# Revit family: Electronics_Community-Point-Source_Biamp_Loudspeaker_IC6_1062
name_source: partatom
category: Communication Devices
units: mm (PartAtom-declared; Revit-internal decimal feet)

## family parameters
Cut with Voids When Loaded = No
Host = Face
Maintain Annotation Orientation = No
OmniClass Number = 23.85.10.11.14.14.14
Part Type = Normal
Room Calculation Point = No
Round Connector Dimension = Use Diameter
Shared = No

## types (4) — shared parameters
Default Elevation = 48 "
Depth = 8.94 "
Description = IC6-1062 High Output 6.5-Inch Two-Way Installation Loudspeaker
Environmental = Outdoor:  IP55W per IEC 60529, MIL-STD-810G
Equalized Maximum SPL = Peak - 119 dB; Continious - 113 dB
Equalized Sensitivity = 1W/1m - 91 dB; 2.83V - 91 dB
Height = 14.29 "
Input Connection = Screw terminal block (5-position)
Manufacturer = Biamp
Mounting Points = M6 threaded rigging points
Nominal Beamwidth  (H x V) = 100° x  100°
Nominal Maximum SPL = Peak - 120 dB; Continious - 114 dB
Nominal Sensitivity = 1W/1m - 92 dB; 2.83V - 92 dB
Operating Environment = Indoor or Weather-Resistant Outdoor
Operating Mode = Low Impedance or 70V/100V models
Operating Range = 56 Hz to 18.5 kHz
Product Documentation Link = https://downloads.biamp.com
Product Page URL = https://www.biamp.com
Product data url = https://www.bimobject.com
Recommended Amplifers = 150W - 300W - 8 ohms,  (35V - 49V)
Transducers = LF 1 x 6.5 (165mm) ferrite driver, 1.5 (37mm) voice coil; HF 1 x 1 (25mm) direct radiating damped fabric dome diaphragm, ferrofuid and heatsink-cooled dual-neodymium motor
URL = https://www.biamp.com
Width = 8 "

## per-type parameters (varying)
| type | Connector Description | Gril Material | Housing Material | Weight |
| IC6-1062/00 B | Screw terminal block (5-position); Low impedance (8 ohm) | Biamp - Plastic - Black(Grid) | Biamp - Plastic - Black | 16.00 lbf |
| IC6-1062/00 W | Screw terminal block (5-position); Low impedance (8 ohm) | Biamp - Plastic - White(Grid) | Biamp - Plastic - White | 16.00 lbf |
| IC6-1062T00 B | Screw terminal block (5-position); 70/100V applications | Biamp - Plastic - Black(Grid) | Biamp - Plastic - Black | 20.00 lbf |
| IC6-1062T00 W | Screw terminal block (5-position); 70/100V applications | Biamp - Plastic - White(Grid) | Biamp - Plastic - White | 20.00 lbf |

note: column(s) folded — value = type name in every type: Model

## geometry (parser evidence)
native form markers: Sweep x2
no freeform markers — native parametric forms only
